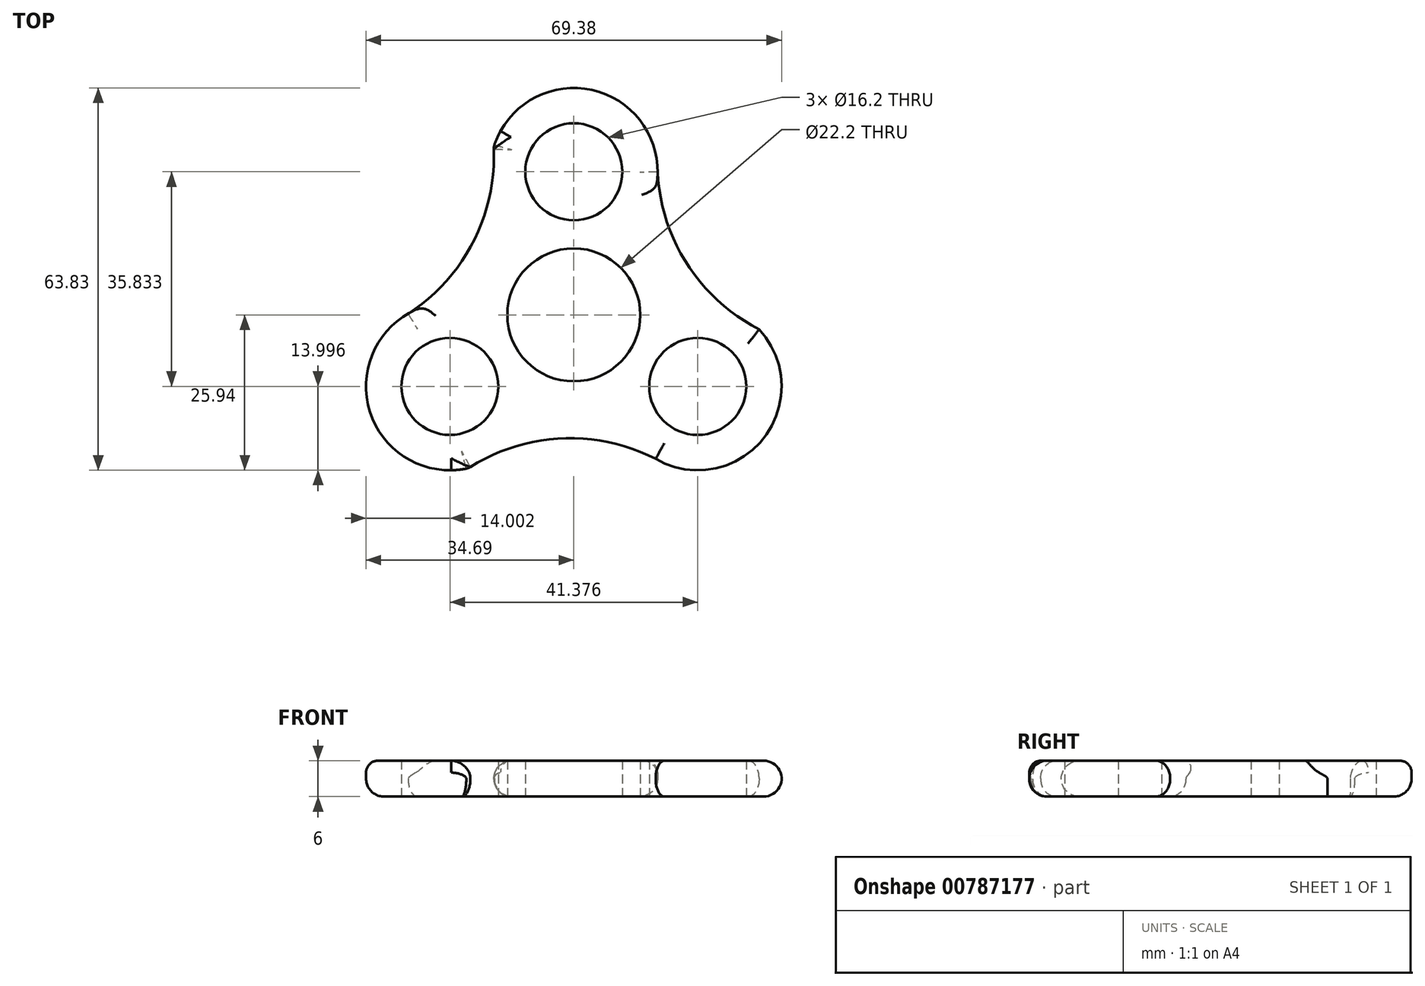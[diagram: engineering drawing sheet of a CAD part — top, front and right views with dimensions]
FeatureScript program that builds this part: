
annotation { "Feature Type Name" : "Feature", "Feature Type Description" : "" }
export const myFeature = defineFeature(function(context is Context, id is Id, definition is map)
    precondition{}
    {
        {
            var Q0;
            Q0=qCreatedBy(makeId("Top.planeOp"),FACE);
            var sketch = newSketch(context, id + "F0", { "sketchPlane" : qUnion([Q0])});
            skCircle(sketch, "E0", {"center": v(0, 0) * mm, "radius": 11.1 * mm});
            skCircle(sketch, "E1", {"center": v(0, 0) * mm, "radius": 3.75 * mm});
            skCircle(sketch, "E2", {"center": v(0, 23.89) * mm, "radius": 8.1 * mm});
            skCircle(sketch, "E3", {"center": v(0, 23.89) * mm, "radius": 3.75 * mm});
            skCircle(sketch, "E4.1.0", {"center": v(-20.69, -11.94) * mm, "radius": 3.75 * mm});
            skCircle(sketch, "E4.1.1", {"center": v(-20.69, -11.94) * mm, "radius": 8.1 * mm});
            skCircle(sketch, "E4.2.0", {"center": v(20.69, -11.94) * mm, "radius": 3.75 * mm});
            skCircle(sketch, "E4.2.1", {"center": v(20.69, -11.94) * mm, "radius": 8.1 * mm});
            skLineSegment(sketch, "E5", {"start": v(-21.01, 24.56) * mm, "end": v(-21.01, 24.56) * mm});
            skArc(sketch, "E6", {"start": v(14, 23.86) * mm, "mid": v(2.1, 37.73) * mm, "end": v(-13.38, 28) * mm});
            skArc(sketch, "E7.1.0", {"start": v(-27.66, 0.2) * mm, "mid": v(-33.72, -17.05) * mm, "end": v(-17.56, -25.6) * mm});
            skArc(sketch, "E7.2.0", {"start": v(13.66, -24.05) * mm, "mid": v(31.63, -20.68) * mm, "end": v(30.94, -2.41) * mm});
            skArc(sketch, "E8", {"start": v(-27.66, 0.2) * mm, "mid": v(-16.79, 12.18) * mm, "end": v(-13.38, 28) * mm});
            skArc(sketch, "E9.1.0", {"start": v(13.66, -24.05) * mm, "mid": v(-2.16, -20.63) * mm, "end": v(-17.56, -25.6) * mm});
            skArc(sketch, "E9.2.0", {"start": v(14, 23.86) * mm, "mid": v(18.94, 8.45) * mm, "end": v(30.94, -2.41) * mm});
            skSolve(sketch);
        }
        {
            var Q0;
            Q0=makeQuery(id+"F0.imprint","IMPRINT",FACE,{"disambiguationData":[TD([[makeQuery(id+"F0.imprint","IMPRINT",EDGE,{"derivedFrom":sQuery(id+"F0.wireOp",EDGE,"E0")}),-1.0]])]});
            extrude(context, id + "F1", {"entities" : qUnion([Q0]), "depth" : 6 * mm, "offsetDistance" : 25 * mm});
        }
        {
            var Q0;
            Q0=makeQuery(id+"F1.opExtrude","CAP_EDGE",EDGE,{"disambiguationData":[OSD([sQuery(id+"F0.wireOp",EDGE,"E9.2.0")])],"isStart":true});
            var Q1;
            Q1=makeQuery(id+"F1.opExtrude","CAP_EDGE",EDGE,{"disambiguationData":[OSD([sQuery(id+"F0.wireOp",EDGE,"E7.2.0")])],"isStart":true});
            var Q2;
            Q2=makeQuery(id+"F1.opExtrude","CAP_EDGE",EDGE,{"disambiguationData":[OSD([sQuery(id+"F0.wireOp",EDGE,"E7.1.0")])],"isStart":true});
            var Q3;
            Q3=makeQuery(id+"F1.opExtrude","CAP_EDGE",EDGE,{"disambiguationData":[OSD([sQuery(id+"F0.wireOp",EDGE,"E6")])],"isStart":true});
            var Q4;
            Q4=makeQuery(id+"F1.opExtrude","CAP_EDGE",EDGE,{"disambiguationData":[OSD([sQuery(id+"F0.wireOp",EDGE,"E9.2.0")])],"isStart":false});
            var Q5;
            Q5=makeQuery(id+"F1.opExtrude","CAP_EDGE",EDGE,{"disambiguationData":[OSD([sQuery(id+"F0.wireOp",EDGE,"E7.2.0")])],"isStart":false});
            var Q6;
            Q6=makeQuery(id+"F1.opExtrude","CAP_EDGE",EDGE,{"disambiguationData":[OSD([sQuery(id+"F0.wireOp",EDGE,"E8")])],"isStart":false});
            fillet(context, id + "F2", {"entities" : qUnion([Q0, Q1, Q2, Q3, Q4, Q5, Q6]), "radius" : 3 * mm, "tangentPropagation" : true, "defaultsChanged" : false, "vertexSettings" : [], "allowEdgeOverflow" : false});
        }
        {
            var Q0;
            Q0=makeQuery(id+"F1.opExtrude","CAP_EDGE",EDGE,{"disambiguationData":[OSD([sQuery(id+"F0.wireOp",EDGE,"E7.1.0")])],"isStart":false});
            var Q1;
            Q1=makeQuery(id+"F1.opExtrude","CAP_EDGE",EDGE,{"disambiguationData":[OSD([sQuery(id+"F0.wireOp",EDGE,"E6")])],"isStart":false});
            fillet(context, id + "F3", {"entities" : qUnion([Q0, Q1]), "radius" : 2 * mm, "tangentPropagation" : true, "allowEdgeOverflow" : false});
        }
    });
